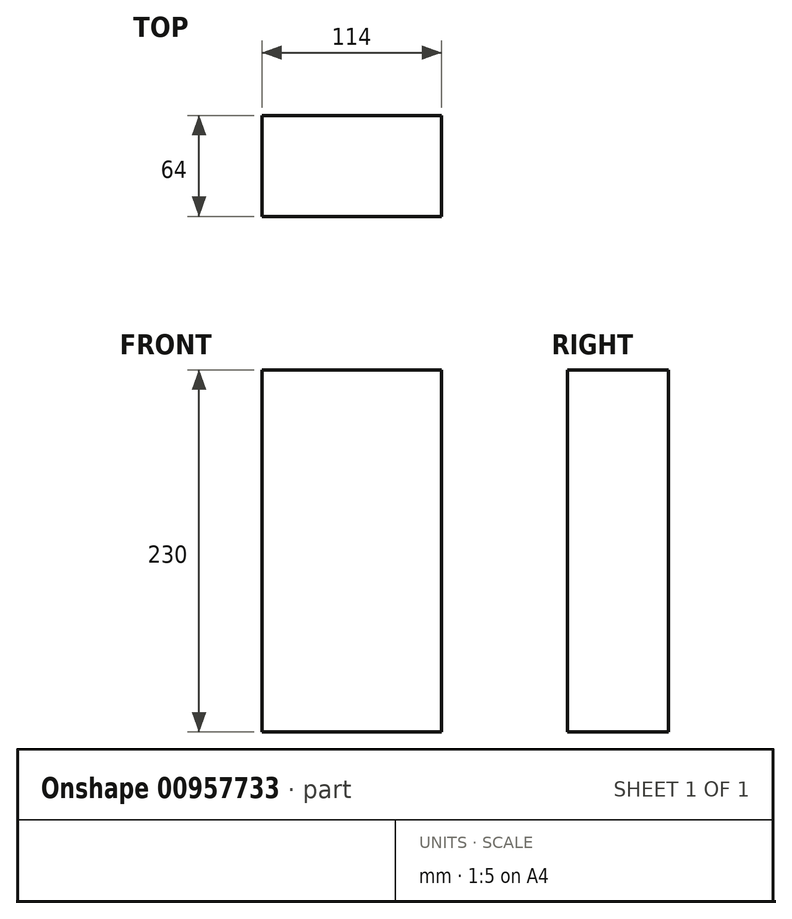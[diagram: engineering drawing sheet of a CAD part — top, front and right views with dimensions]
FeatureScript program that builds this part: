
annotation { "Feature Type Name" : "Feature", "Feature Type Description" : "" }
export const myFeature = defineFeature(function(context is Context, id is Id, definition is map)
    precondition{}
    {
        {
            var Q0;
            Q0=qCreatedBy(makeId("Top.planeOp"),FACE);
            var sketch = newSketch(context, id + "F0", { "sketchPlane" : qUnion([Q0])});
            skLineSegment(sketch, "E0.bottom", {"start": v(-57, -32) * mm, "end": v(57, -32) * mm});
            skLineSegment(sketch, "E0.top", {"start": v(-57, 32) * mm, "end": v(57, 32) * mm});
            skLineSegment(sketch, "E0.left", {"start": v(-57, -32) * mm, "end": v(-57, 32) * mm});
            skLineSegment(sketch, "E0.right", {"start": v(57, -32) * mm, "end": v(57, 32) * mm});
            skPoint(sketch, "E0.middle", {"position": v(0, 0) * mm});
            skSolve(sketch);
        }
        {
            var Q0;
            Q0=qSketchRegion(id+"F0",true);
            extrude(context, id + "F1", {"entities" : qUnion([Q0]), "depth" : 230 * mm, "offsetDistance" : 25 * mm});
        }
    });
